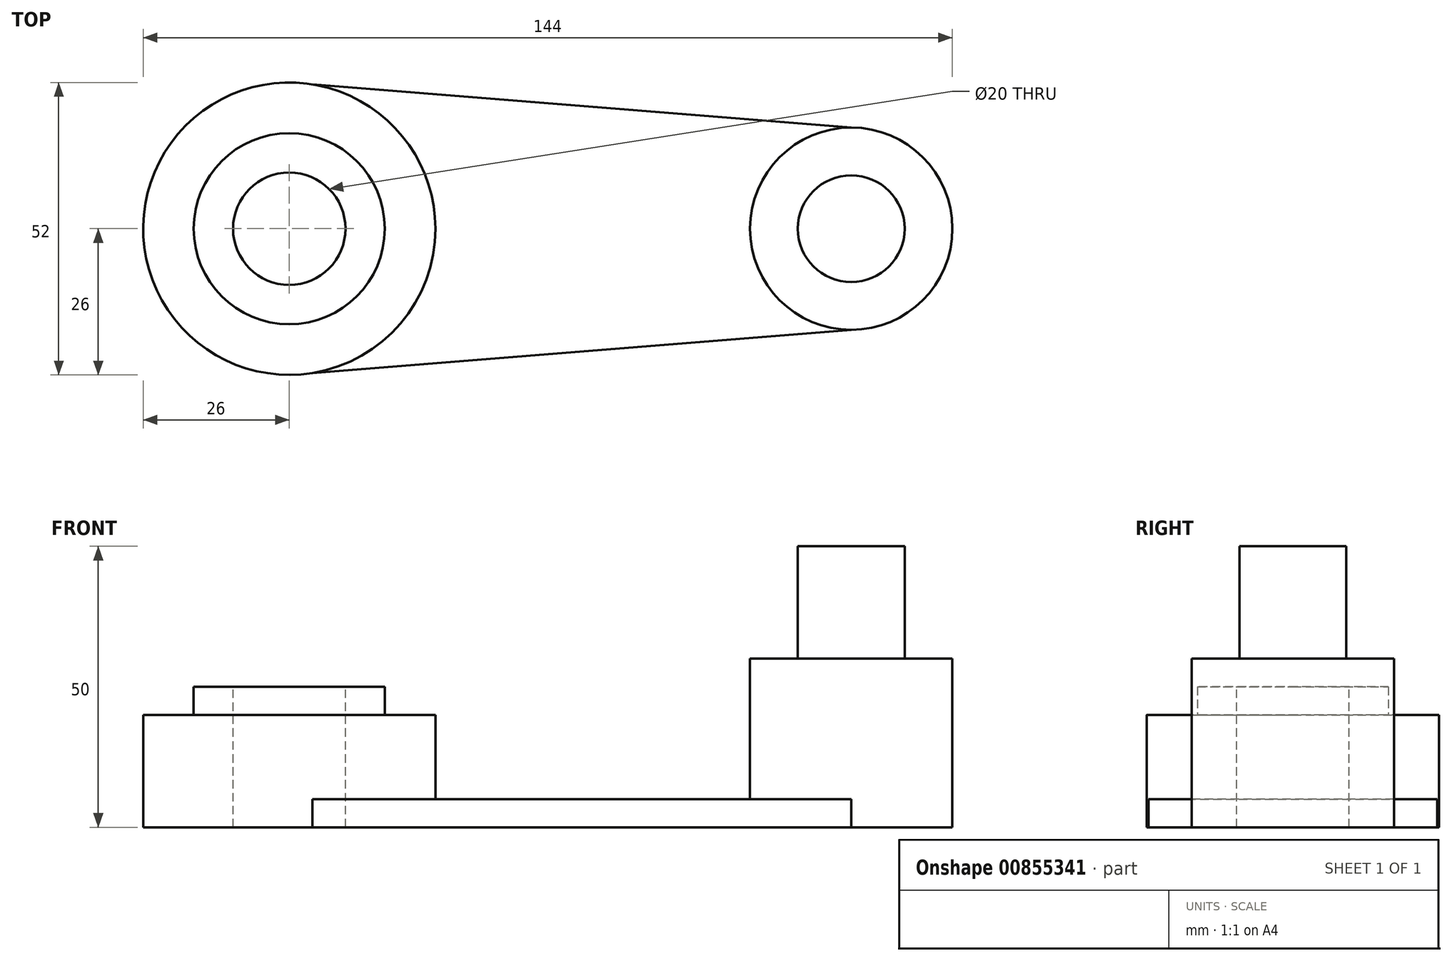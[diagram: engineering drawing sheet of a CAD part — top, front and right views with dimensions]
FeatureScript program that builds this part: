
annotation { "Feature Type Name" : "Feature", "Feature Type Description" : "" }
export const myFeature = defineFeature(function(context is Context, id is Id, definition is map)
    precondition{}
    {
        {
            var Q0;
            Q0=qCreatedBy(makeId("Top.planeOp"),FACE);
            var sketch = newSketch(context, id + "F0", { "sketchPlane" : qUnion([Q0])});
            skCircle(sketch, "E0", {"center": v(0, 0) * mm, "radius": 26 * mm});
            skSolve(sketch);
        }
        {
            var Q0;
            Q0=qCreatedBy(makeId("Top.planeOp"),FACE);
            var sketch = newSketch(context, id + "F1", { "sketchPlane" : qUnion([Q0])});
            skLineSegment(sketch, "E1", {"start": v(0, 26) * mm, "end": v(100, 18) * mm});
            skLineSegment(sketch, "E2", {"start": v(0, -26) * mm, "end": v(100, -18) * mm});
            skPoint(sketch, "E3.startSnap0", {"position": v(100, 0) * mm});
            skLineSegment(sketch, "E4", {"start": v(0, -26) * mm, "end": v(0, 26) * mm});
            skLineSegment(sketch, "E5", {"start": v(100, 18) * mm, "end": v(100, -18) * mm});
            skSolve(sketch);
        }
        {
            var Q0;
            Q0=qCreatedBy(makeId("Top.planeOp"),FACE);
            var sketch = newSketch(context, id + "F2", { "sketchPlane" : qUnion([Q0])});
            skCircle(sketch, "E6", {"center": v(100, 0) * mm, "radius": 18 * mm});
            skSolve(sketch);
        }
        {
            var Q0;
            Q0=qSketchRegion(id+"F0",true);
            extrude(context, id + "F3", {"entities" : qUnion([Q0]), "depth" : 20 * mm, "offsetDistance" : 25 * mm});
        }
        {
            var Q0;
            Q0=qSketchRegion(id+"F1",true);
            extrude(context, id + "F4", {"entities" : qUnion([Q0]), "operationType" : NewBodyOperationType.ADD, "depth" : 5 * mm, "offsetDistance" : 25 * mm});
        }
        {
            var Q0;
            Q0=makeQuery(id+"F2.imprint","IMPRINT",FACE,{"disambiguationData":[TD([[makeQuery(id+"F2.imprint","IMPRINT",EDGE,{"derivedFrom":sQuery(id+"F2.wireOp",EDGE,"E6")}),1.0]])]});
            extrude(context, id + "F5", {"entities" : qUnion([Q0]), "operationType" : NewBodyOperationType.ADD, "depth" : 30 * mm, "offsetDistance" : 25 * mm});
        }
        {
            var Q0;
            Q0=makeQuery(id+"F3.opExtrude","CAP_FACE",FACE,{"disambiguationData":[OSD([sQuery(id+"F0.wireOp",EDGE,"E0")])],"isStart":false});
            var sketch = newSketch(context, id + "F6", { "sketchPlane" : qUnion([Q0])});
            skCircle(sketch, "E7", {"center": v(0, 0) * mm, "radius": 17 * mm});
            skSolve(sketch);
        }
        {
            var Q0;
            Q0=makeQuery(id+"F5.opExtrude","CAP_FACE",FACE,{"disambiguationData":[OSD([sQuery(id+"F2.wireOp",EDGE,"E6")])],"isStart":false});
            var sketch = newSketch(context, id + "F7", { "sketchPlane" : qUnion([Q0])});
            skCircle(sketch, "E8", {"center": v(100, 0) * mm, "radius": 9.5 * mm});
            skSolve(sketch);
        }
        {
            var Q0;
            Q0=makeQuery(id+"F6.imprint","IMPRINT",FACE,{"disambiguationData":[TD([[makeQuery(id+"F6.imprint","IMPRINT",EDGE,{"derivedFrom":sQuery(id+"F6.wireOp",EDGE,"E7")}),1.0]])]});
            extrude(context, id + "F8", {"entities" : qUnion([Q0]), "operationType" : NewBodyOperationType.ADD, "depth" : 5 * mm, "offsetDistance" : 25 * mm});
        }
        {
            var Q0;
            Q0=makeQuery(id+"F7.imprint","IMPRINT",FACE,{"disambiguationData":[TD([[makeQuery(id+"F7.imprint","IMPRINT",EDGE,{"derivedFrom":sQuery(id+"F7.wireOp",EDGE,"E8")}),1.0]])]});
            extrude(context, id + "F9", {"entities" : qUnion([Q0]), "operationType" : NewBodyOperationType.ADD, "depth" : 20 * mm, "offsetDistance" : 25 * mm});
        }
        {
            var Q0;
            Q0=makeQuery(id+"F8.opExtrude","CAP_FACE",FACE,{"disambiguationData":[OSD([sQuery(id+"F6.wireOp",EDGE,"E7")])],"isStart":false});
            var sketch = newSketch(context, id + "F10", { "sketchPlane" : qUnion([Q0])});
            skCircle(sketch, "E9", {"center": v(0, 0) * mm, "radius": 10 * mm});
            skSolve(sketch);
        }
        {
            var Q0;
            Q0=makeQuery(id+"F10.imprint","IMPRINT",FACE,{"disambiguationData":[TD([[makeQuery(id+"F10.imprint","IMPRINT",EDGE,{"derivedFrom":sQuery(id+"F10.wireOp",EDGE,"E9")}),1.0]])]});
            extrude(context, id + "F11", {"entities" : qUnion([Q0]), "operationType" : NewBodyOperationType.REMOVE, "endBound" : BoundingType.UP_TO_NEXT, "oppositeDirection" : true, "depth" : 25 * mm, "offsetDistance" : 25 * mm});
        }
    });
